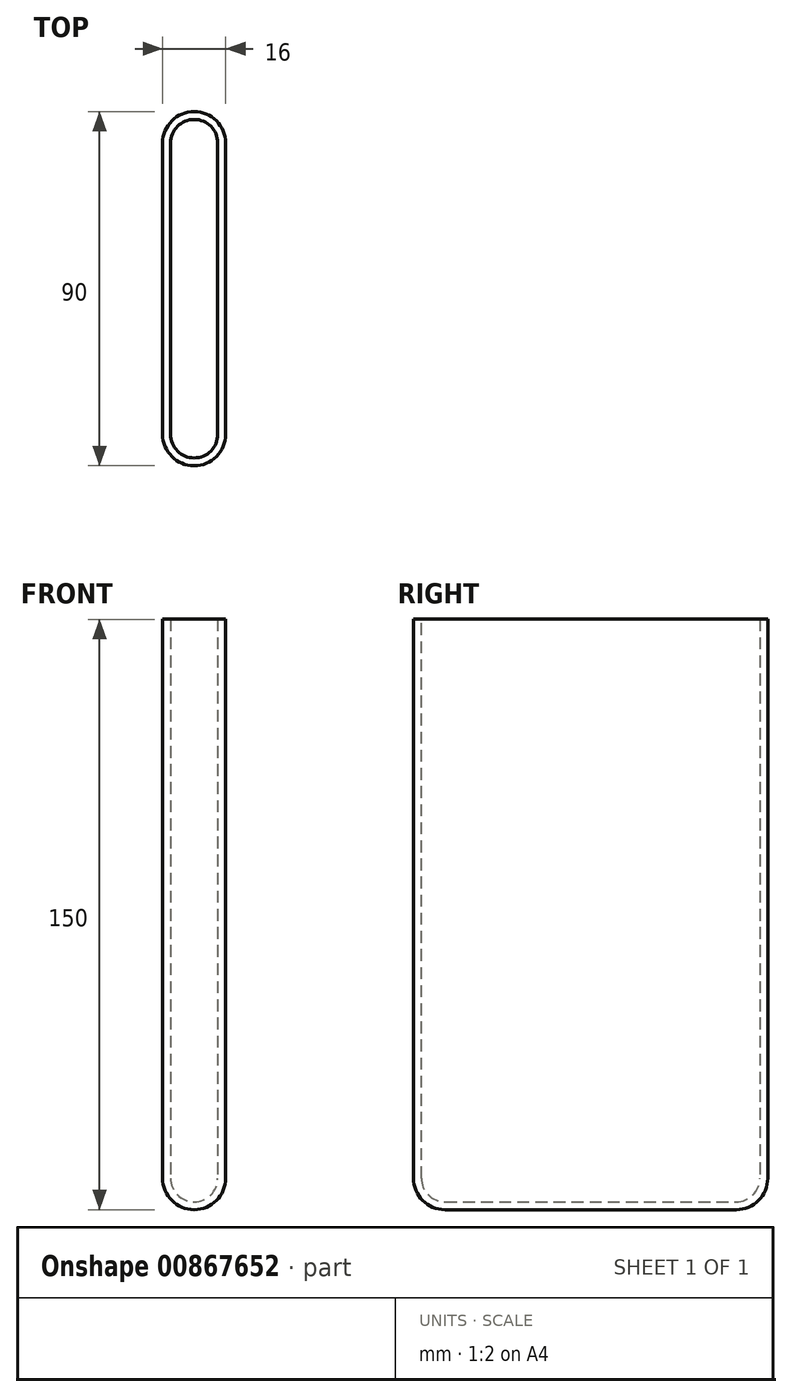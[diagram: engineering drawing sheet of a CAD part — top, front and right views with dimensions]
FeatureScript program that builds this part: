
annotation { "Feature Type Name" : "Feature", "Feature Type Description" : "" }
export const myFeature = defineFeature(function(context is Context, id is Id, definition is map)
    precondition{}
    {
        {
            var Q0;
            Q0=qCreatedBy(makeId("Front.planeOp"),FACE);
            var sketch = newSketch(context, id + "F0", { "sketchPlane" : qUnion([Q0])});
            skLineSegment(sketch, "E0.bottom", {"start": v(0, 69.11) * mm, "end": v(16, 69.11) * mm});
            skLineSegment(sketch, "E0.top", {"start": v(0, -80.89) * mm, "end": v(16, -80.89) * mm});
            skLineSegment(sketch, "E0.left", {"start": v(0, 69.11) * mm, "end": v(0, -80.89) * mm});
            skLineSegment(sketch, "E0.right", {"start": v(16, 69.11) * mm, "end": v(16, -80.89) * mm});
            skPoint(sketch, "E1.MirrorCS.end.orphan", {"position": v(16, 69.11) * mm});
            skPoint(sketch, "E1.MirrorCS.start.orphan", {"position": v(32, 69.11) * mm});
            skPoint(sketch, "E2.MirrorCS.end.orphan", {"position": v(16, -80.89) * mm});
            skPoint(sketch, "E2.MirrorCS.start.orphan", {"position": v(32, -80.89) * mm});
            skSolve(sketch);
        }
        {
            var Q0;
            Q0=makeQuery(id+"F0.imprint","IMPRINT",FACE,{"disambiguationData":[TD([[makeQuery(id+"F0.imprint","IMPRINT",EDGE,{"derivedFrom":sQuery(id+"F0.wireOp",EDGE,"E0.bottom")}),-1.0]])]});
            extrude(context, id + "F1", {"entities" : qUnion([Q0]), "endBound" : BoundingType.SYMMETRIC, "depth" : 90 * mm, "offsetDistance" : 25 * mm});
        }
        {
            var Q0;
            Q0=makeQuery(id+"F1.opExtrude","CAP_EDGE",EDGE,{"disambiguationData":[OSD([sQuery(id+"F0.wireOp",EDGE,"E0.left")])],"isStart":false});
            var Q1;
            Q1=makeQuery(id+"F1.opExtrude","CAP_EDGE",EDGE,{"disambiguationData":[OSD([sQuery(id+"F0.wireOp",EDGE,"E0.right")])],"isStart":false});
            var Q2;
            Q2=makeQuery(id+"F1.opExtrude","SWEPT_EDGE",EDGE,{"disambiguationData":[OSD([sQuery(id+"F0.wireOp",EDGE,"E0.top"),sQuery(id+"F0.wireOp",EDGE,"E0.right")])]});
            var Q3;
            Q3=makeQuery(id+"F1.opExtrude","SWEPT_EDGE",EDGE,{"disambiguationData":[OSD([sQuery(id+"F0.wireOp",EDGE,"E0.top"),sQuery(id+"F0.wireOp",EDGE,"E0.left")])]});
            var Q4;
            Q4=makeQuery(id+"F1.opExtrude","CAP_EDGE",EDGE,{"disambiguationData":[OSD([sQuery(id+"F0.wireOp",EDGE,"E0.right")])],"isStart":true});
            var Q5;
            Q5=makeQuery(id+"F1.opExtrude","CAP_EDGE",EDGE,{"disambiguationData":[OSD([sQuery(id+"F0.wireOp",EDGE,"E0.left")])],"isStart":true});
            var Q6;
            Q6=makeQuery(id+"F1.opExtrude","CAP_EDGE",EDGE,{"disambiguationData":[OSD([sQuery(id+"F0.wireOp",EDGE,"E0.top")])],"isStart":true});
            var Q7;
            Q7=makeQuery(id+"F1.opExtrude","SWEPT_FACE",FACE,{"disambiguationData":[OSD([sQuery(id+"F0.wireOp",EDGE,"E0.top")])]});
            fillet(context, id + "F2", {"entities" : qUnion([Q0, Q1, Q2, Q3, Q4, Q5, Q6, Q7]), "radius" : 8 * mm, "tangentPropagation" : true, "allowEdgeOverflow" : false});
        }
        {
            var Q0;
            Q0=makeQuery(id+"F1.opExtrude","SWEPT_FACE",FACE,{"disambiguationData":[OSD([sQuery(id+"F0.wireOp",EDGE,"E0.bottom")])]});
            shell(context, id + "F3", {"entities" : qUnion([Q0]), "thickness" : 2 * mm});
        }
    });
